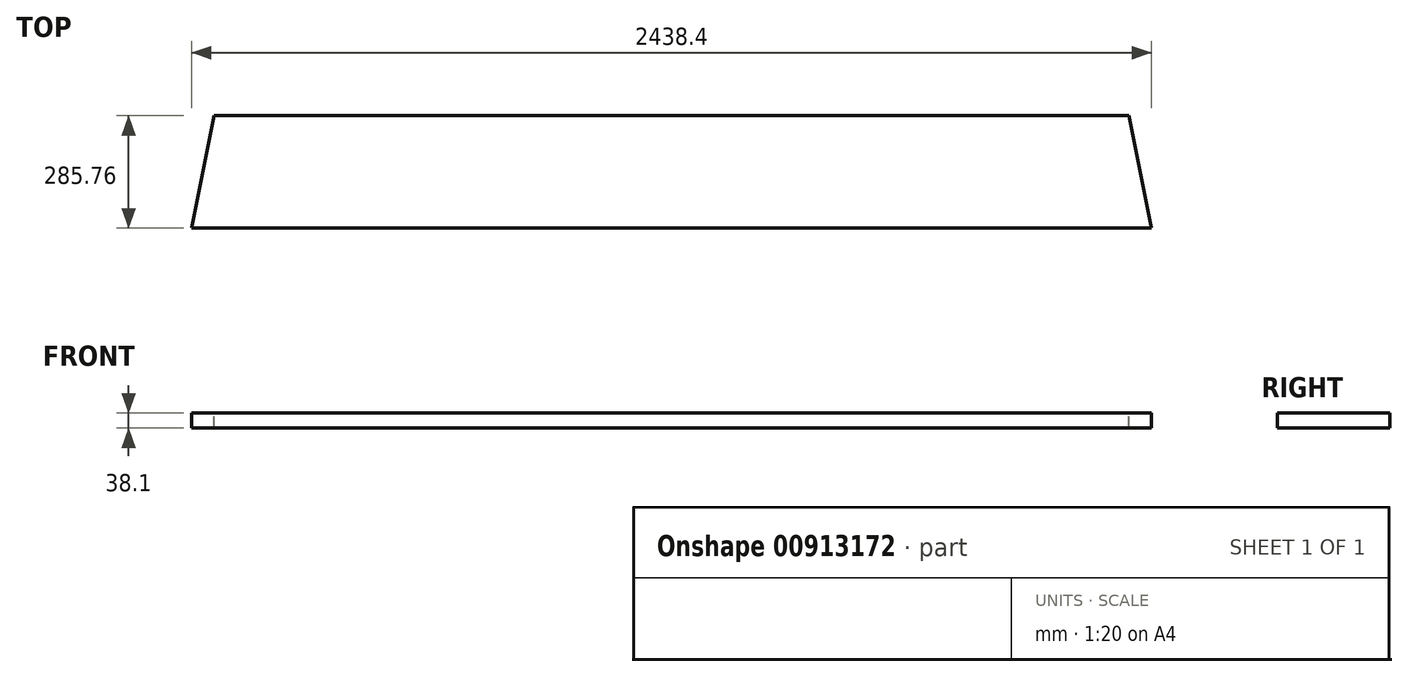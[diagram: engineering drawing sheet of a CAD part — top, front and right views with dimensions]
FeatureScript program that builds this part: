
annotation { "Feature Type Name" : "Feature", "Feature Type Description" : "" }
export const myFeature = defineFeature(function(context is Context, id is Id, definition is map)
    precondition{}
    {
        {
            var Q0;
            Q0=qCreatedBy(makeId("Top.planeOp"),FACE);
            var sketch = newSketch(context, id + "F0", { "sketchPlane" : qUnion([Q0])});
            skLineSegment(sketch, "E0.bottom", {"start": v(-1162.36, 142.88) * mm, "end": v(1162.36, 142.88) * mm});
            skLineSegment(sketch, "E0.top", {"start": v(-1219.2, -142.88) * mm, "end": v(1219.2, -142.88) * mm});
            skLineSegment(sketch, "E0.left", {"start": v(-1162.36, 142.88) * mm, "end": v(-1219.2, -142.88) * mm});
            skLineSegment(sketch, "E0.right", {"start": v(1162.36, 142.88) * mm, "end": v(1219.2, -142.88) * mm});
            skLineSegment(sketch, "E1", {"start": v(-1190.78, 0) * mm, "end": v(0, 0) * mm, "construction": true});
            skLineSegment(sketch, "E2", {"start": v(0, 0) * mm, "end": v(1190.78, 0) * mm, "construction": true});
            skLineSegment(sketch, "E3", {"start": v(0, 142.88) * mm, "end": v(0, 0) * mm, "construction": true});
            skLineSegment(sketch, "E4", {"start": v(0, 0) * mm, "end": v(0, -142.88) * mm, "construction": true});
            skSolve(sketch);
        }
        {
            var Q0;
            Q0=makeQuery(id+"F0.imprint","IMPRINT",FACE,{"disambiguationData":[TD([[makeQuery(id+"F0.imprint","IMPRINT",EDGE,{"derivedFrom":sQuery(id+"F0.wireOp",EDGE,"E0.bottom")}),-1.0]])]});
            extrude(context, id + "F1", {"entities" : qUnion([Q0]), "oppositeDirection" : true, "depth" : 38.1 * mm, "offsetDistance" : 25.4 * mm});
        }
    });
